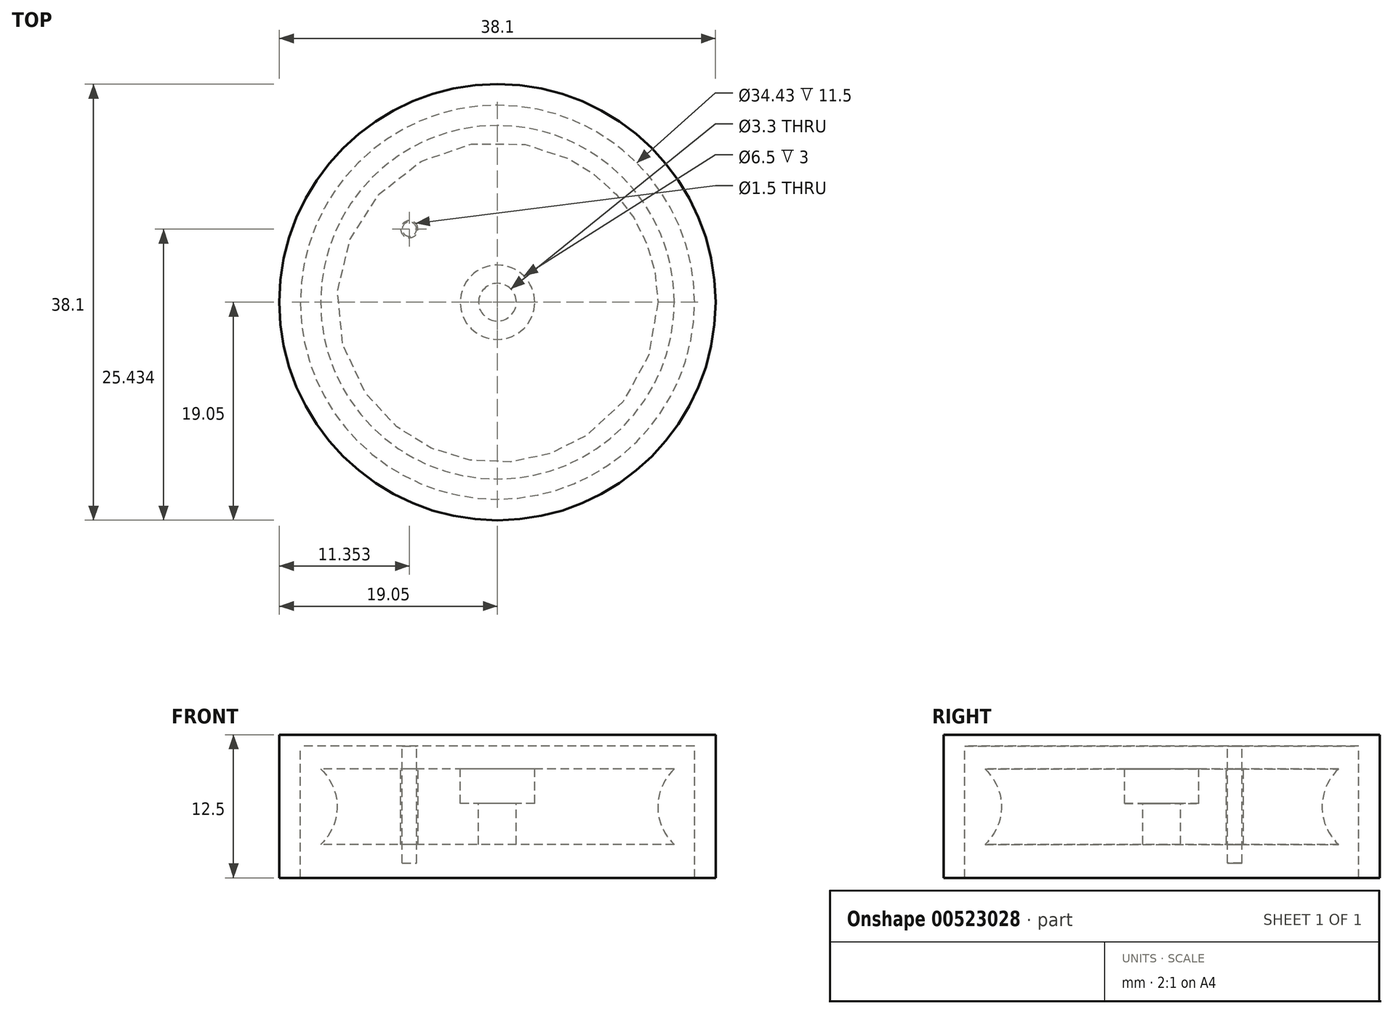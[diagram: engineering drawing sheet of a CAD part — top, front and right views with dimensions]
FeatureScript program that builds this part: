
annotation { "Feature Type Name" : "Feature", "Feature Type Description" : "" }
export const myFeature = defineFeature(function(context is Context, id is Id, definition is map)
    precondition{}
    {
        {
            var Q0;
            Q0=qCreatedBy(makeId("Front.planeOp"),FACE);
            var sketch = newSketch(context, id + "F0", { "sketchPlane" : qUnion([Q0])});
            skArc(sketch, "E0", {"start": v(-15.45, -3.3) * mm, "mid": v(-14, 0) * mm, "end": v(-15.45, 3.3) * mm});
            skLineSegment(sketch, "E1", {"start": v(-15.45, 3.3) * mm, "end": v(0, 3.3) * mm});
            skLineSegment(sketch, "E2", {"start": v(0, 3.3) * mm, "end": v(0, -3.3) * mm});
            skLineSegment(sketch, "E3", {"start": v(0, -3.3) * mm, "end": v(-15.45, -3.3) * mm});
            skSolve(sketch);
        }
        {
            var Q0;
            Q0=makeQuery(id+"F0.imprint","IMPRINT",FACE,{"disambiguationData":[TD([[makeQuery(id+"F0.imprint","IMPRINT",EDGE,{"derivedFrom":sQuery(id+"F0.wireOp",EDGE,"E0")}),-1.0]])]});
            var Q1;
            Q1=sQuery(id+"F0.wireOp",EDGE,"E2");
            revolve(context, id + "F1", {"entities" : qUnion([Q0]), "axis" : qUnion([Q1]), "revolveType" : RevolveType.FULL});
        }
        {
            var Q0;
            Q0=makeQuery(id+"F1.opRevolve","SWEPT_FACE",FACE,{"disambiguationData":[OSD([sQuery(id+"F0.wireOp",EDGE,"E1")])]});
            cPlane(context, id + "F2", {"entities" : qUnion([Q0]), "cplaneType" : CPlaneType.OFFSET, "offset" : 0 * mm, "width" : 150 * mm, "height" : 150 * mm});
        }
        {
            var Q0;
            Q0=qCreatedBy(id+"F2.planeOp",FACE);
            var sketch = newSketch(context, id + "F3", { "sketchPlane" : qUnion([Q0])});
            skCircle(sketch, "E4.0.0", {"center": v(0, 0) * mm, "radius": 15.45 * mm});
            skCircle(sketch, "E5", {"center": v(-7.7, 6.38) * mm, "radius": 0.75 * mm});
            skSolve(sketch);
        }
        {
            var Q0;
            Q0=sQuery(id+"F3.wireOp",VERTEX,"E4.0.0.center");
            var Q1;
            Q1=makeQuery(id+"F1.opRevolve","SWEPT_BODY",BODY,{"disambiguationData":[OSD([sQuery(id+"F0.wireOp",EDGE,"E0"),sQuery(id+"F0.wireOp",EDGE,"E1"),sQuery(id+"F0.wireOp",EDGE,"E2"),sQuery(id+"F0.wireOp",EDGE,"E3")])]});
            hole(context, id + "F4", {"style" : HoleStyle.C_BORE, "endStyle" : HoleEndStyle.THROUGH, "standardTappedOrClearance" : lookupTablePath({ "standard" : "ISO", "fit" : "Normal", "size" : "M3", "type" : "Clearance" }), "standardBlindInLast" : lookupTablePath({ "fit" : "Standard", "standard" : "ISO", "size" : "M3", "type" : "Clearance" }), "holeDiameter" : 3.3 * mm, "cBoreDiameter" : 6.5 * mm, "cBoreDepth" : 3 * mm, "isTappedThrough" : true, "tappedDepth" : 12 * mm, "tapClearance" : 3, "locations" : qUnion([Q0]), "scope" : qUnion([Q1])});
        }
        {
            var Q0;
            Q0=makeQuery(id+"F3.imprint","IMPRINT",FACE,{"disambiguationData":[TD([[makeQuery(id+"F3.imprint","IMPRINT",EDGE,{"derivedFrom":sQuery(id+"F3.wireOp",EDGE,"E5")}),1.0]])]});
            extrude(context, id + "F5", {"entities" : qUnion([Q0]), "operationType" : NewBodyOperationType.REMOVE, "oppositeDirection" : true, "depth" : 25 * mm, "offsetDistance" : 25 * mm});
        }
        {
            var Q0;
            Q0=makeQuery(id+"F3.imprint","IMPRINT",FACE,{"disambiguationData":[TD([[makeQuery(id+"F3.imprint","IMPRINT",EDGE,{"derivedFrom":sQuery(id+"F3.wireOp",EDGE,"E4.0.0")}),1.0]])]});
            cPlane(context, id + "F6", {"entities" : qUnion([Q0]), "cplaneType" : CPlaneType.OFFSET, "offset" : 3 * mm, "width" : 150 * mm, "height" : 150 * mm});
        }
        {
            var Q0;
            Q0=qCreatedBy(id+"F6.planeOp",FACE);
            var sketch = newSketch(context, id + "F7", { "sketchPlane" : qUnion([Q0])});
            skCircle(sketch, "E6", {"center": v(0, 0) * mm, "radius": 17.21 * mm});
            skCircle(sketch, "E7", {"center": v(0, 0) * mm, "radius": 19.05 * mm});
            skSolve(sketch);
        }
        {
            var Q0;
            Q0=makeQuery(id+"F7.imprint","IMPRINT",FACE,{"disambiguationData":[TD([[makeQuery(id+"F7.imprint","IMPRINT",EDGE,{"derivedFrom":sQuery(id+"F7.wireOp",EDGE,"E6")}),-1.0]])]});
            var Q1;
            Q1=sQuery(id+"F7.wireOp",EDGE,"E6");
            var Q2;
            Q2=sQuery(id+"F7.wireOp",EDGE,"E7");
            extrude(context, id + "F8", {"entities" : qUnion([Q0]), "surfaceEntities" : qUnion([Q1, Q2]), "oppositeDirection" : true, "depth" : 12.5 * mm, "offsetDistance" : 25 * mm});
        }
        {
            var Q0;
            Q0=makeQuery(id+"F7.imprint","IMPRINT",FACE,{"disambiguationData":[TD([[makeQuery(id+"F7.imprint","IMPRINT",EDGE,{"derivedFrom":sQuery(id+"F7.wireOp",EDGE,"E6")}),1.0]])]});
            extrude(context, id + "F9", {"entities" : qUnion([Q0]), "operationType" : NewBodyOperationType.ADD, "oppositeDirection" : true, "depth" : 1 * mm, "offsetDistance" : 25 * mm});
        }
        {
            var Q0;
            Q0=makeQuery(id+"F9.opExtrude","CAP_FACE",FACE,{"disambiguationData":[OSD([sQuery(id+"F7.wireOp",EDGE,"E6")])],"isStart":false});
            cPlane(context, id + "F10", {"entities" : qUnion([Q0]), "cplaneType" : CPlaneType.OFFSET, "offset" : 0 * mm, "width" : 150 * mm, "height" : 150 * mm});
        }
        {
            var Q0;
            Q0=qCreatedBy(id+"F10.planeOp",FACE);
            var sketch = newSketch(context, id + "F11", { "sketchPlane" : qUnion([Q0])});
            skCircle(sketch, "E8.0", {"center": v(-7.7, -6.38) * mm, "radius": 0.62 * mm});
            skSolve(sketch);
        }
        {
            var Q0;
            Q0 = qSketchRegion(id + "F11", true);
            extrude(context, id + "F12", {"entities" : qUnion([Q0]), "depth" : 10.2 * mm, "offsetDistance" : 25 * mm});
        }
    });
